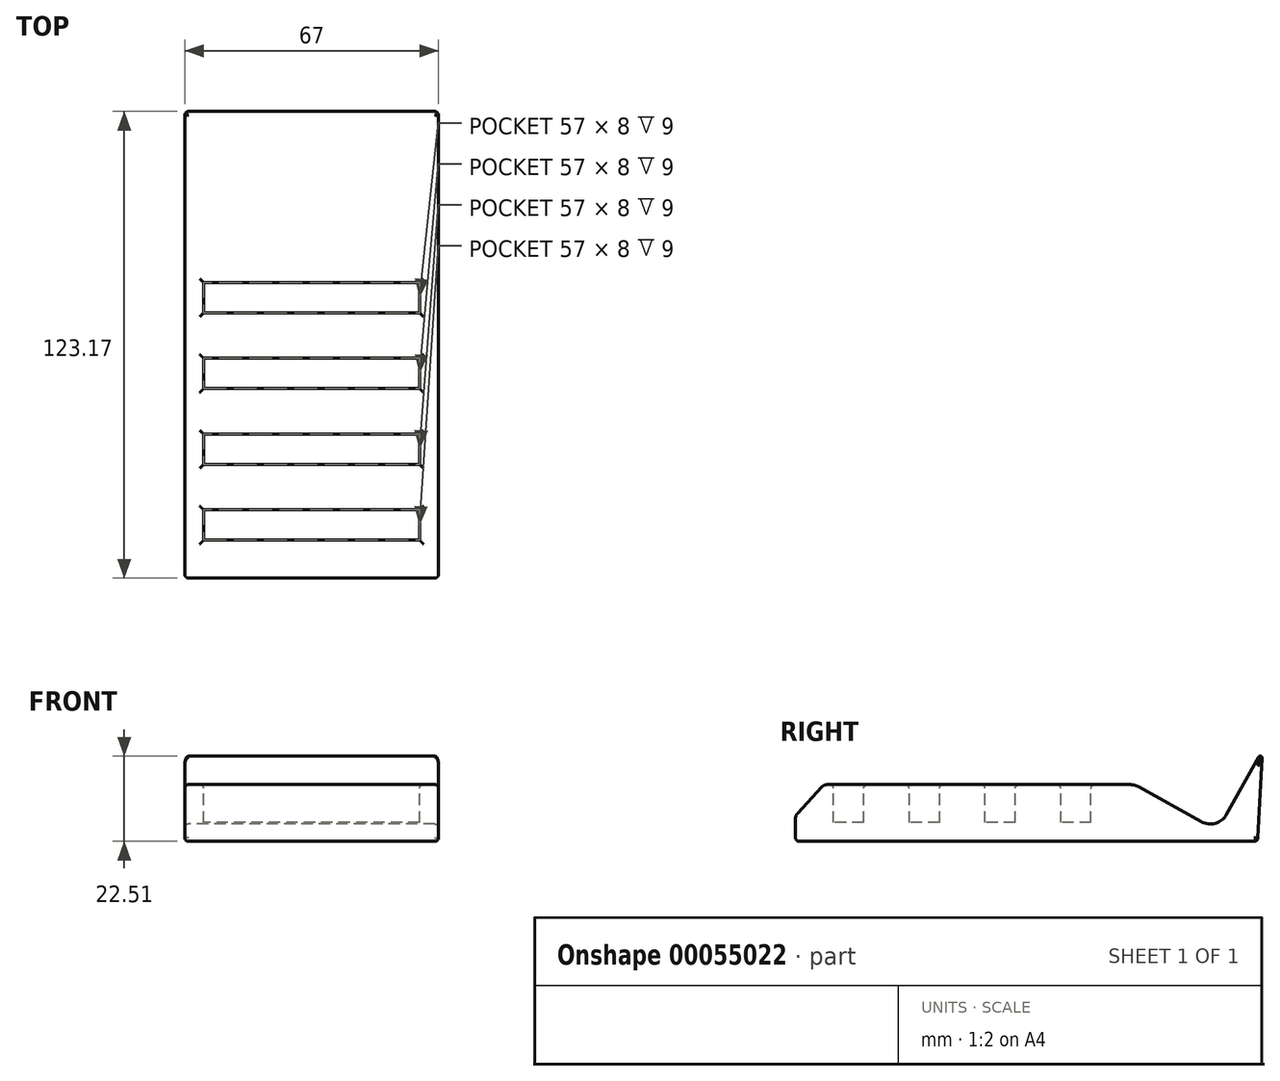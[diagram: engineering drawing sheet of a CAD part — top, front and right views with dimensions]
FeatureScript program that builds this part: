
annotation { "Feature Type Name" : "Feature", "Feature Type Description" : "" }
export const myFeature = defineFeature(function(context is Context, id is Id, definition is map)
    precondition{}
    {
        {
            var Q0;
            Q0=qCreatedBy(makeId("Right.planeOp"),FACE);
            var sketch = newSketch(context, id + "F0", { "sketchPlane" : qUnion([Q0])});
            skLineSegment(sketch, "E0.rect.bottom", {"start": v(27.22, 7.5) * mm, "end": v(-52.62, 7.5) * mm});
            skLineSegment(sketch, "E0.rect.top", {"start": v(61, -7.5) * mm, "end": v(-61, -7.5) * mm});
            skLineSegment(sketch, "E0.rect.right", {"start": v(-61, -1.4) * mm, "end": v(-61, -7.5) * mm});
            skPoint(sketch, "E0.rect.middle", {"position": v(0, 0) * mm});
            skLineSegment(sketch, "E1", {"start": v(45.97, -2.27) * mm, "end": v(29.66, 6.86) * mm});
            skLineSegment(sketch, "E2", {"start": v(52.78, -0.35) * mm, "end": v(61.24, 14.76) * mm});
            skLineSegment(sketch, "E3", {"start": v(61, -7.5) * mm, "end": v(62.17, 14.49) * mm});
            skPoint(sketch, "E4.visualSharp", {"position": v(62.29, 16.63) * mm});
            skArc(sketch, "E4.filletArc", {"start": v(62.17, 14.49) * mm, "mid": v(61.81, 15) * mm, "end": v(61.24, 14.76) * mm});
            skPoint(sketch, "E5.visualSharp", {"position": v(28.52, 7.5) * mm});
            skArc(sketch, "E5.filletArc", {"start": v(29.66, 6.86) * mm, "mid": v(28.48, 7.34) * mm, "end": v(27.22, 7.5) * mm});
            skPoint(sketch, "E6.visualSharp", {"position": v(50.33, -4.72) * mm});
            skArc(sketch, "E6.filletArc", {"start": v(45.97, -2.27) * mm, "mid": v(49.77, -2.72) * mm, "end": v(52.78, -0.35) * mm});
            skLineSegment(sketch, "E7", {"start": v(-60.47, -0.05) * mm, "end": v(-54.1, 6.86) * mm});
            skPoint(sketch, "E8.visualSharp", {"position": v(-53.5, 7.5) * mm});
            skArc(sketch, "E8.filletArc", {"start": v(-52.62, 7.5) * mm, "mid": v(-53.43, 7.33) * mm, "end": v(-54.1, 6.86) * mm});
            skPoint(sketch, "E9.visualSharp", {"position": v(-61, -0.62) * mm});
            skArc(sketch, "E9.filletArc", {"start": v(-60.47, -0.05) * mm, "mid": v(-60.86, -0.67) * mm, "end": v(-61, -1.4) * mm});
            skSolve(sketch);
        }
        {
            var Q0;
            Q0=makeQuery(id+"F0.imprint","IMPRINT",FACE,{"disambiguationData":[TD([[makeQuery(id+"F0.imprint","IMPRINT",EDGE,{"derivedFrom":sQuery(id+"F0.wireOp",EDGE,"E0.rect.bottom")}),1.0]])]});
            extrude(context, id + "F1", {"entities" : qUnion([Q0]), "depth" : 33.5 * mm, "hasSecondDirection" : true, "secondDirectionOppositeDirection" : true, "secondDirectionDepth" : 33.5 * mm});
        }
        {
            var Q0;
            Q0=makeQuery(id+"F1.opExtrude","SWEPT_FACE",FACE,{"disambiguationData":[OSD([sQuery(id+"F0.wireOp",EDGE,"E0.rect.bottom")])]});
            var sketch = newSketch(context, id + "F2", { "sketchPlane" : qUnion([Q0])});
            skLineSegment(sketch, "E10.rect.bottom", {"start": v(28.5, -43) * mm, "end": v(-28.5, -43) * mm});
            skLineSegment(sketch, "E10.rect.top", {"start": v(28.5, -51) * mm, "end": v(-28.5, -51) * mm});
            skLineSegment(sketch, "E10.rect.left", {"start": v(28.5, -43) * mm, "end": v(28.5, -51) * mm});
            skLineSegment(sketch, "E10.rect.right", {"start": v(-28.5, -43) * mm, "end": v(-28.5, -51) * mm});
            skPoint(sketch, "E10.rect.middle", {"position": v(0, -47) * mm});
            skPoint(sketch, "E11.rect.middle", {"position": v(0, -27) * mm});
            skLineSegment(sketch, "E11.rect.bottom", {"start": v(28.5, -23) * mm, "end": v(-28.5, -23) * mm});
            skLineSegment(sketch, "E11.rect.right", {"start": v(-28.5, -23) * mm, "end": v(-28.5, -31) * mm});
            skLineSegment(sketch, "E11.rect.left", {"start": v(28.5, -23) * mm, "end": v(28.5, -31) * mm});
            skLineSegment(sketch, "E11.rect.top", {"start": v(28.5, -31) * mm, "end": v(-28.5, -31) * mm});
            skPoint(sketch, "E12.rect.middle", {"position": v(0, -7) * mm});
            skLineSegment(sketch, "E12.rect.bottom", {"start": v(28.5, -3) * mm, "end": v(-28.5, -3) * mm});
            skLineSegment(sketch, "E12.rect.right", {"start": v(-28.5, -3) * mm, "end": v(-28.5, -11) * mm});
            skLineSegment(sketch, "E12.rect.left", {"start": v(28.5, -3) * mm, "end": v(28.5, -11) * mm});
            skLineSegment(sketch, "E12.rect.top", {"start": v(28.5, -11) * mm, "end": v(-28.5, -11) * mm});
            skPoint(sketch, "E13.rect.middle", {"position": v(0, 13) * mm});
            skLineSegment(sketch, "E13.rect.bottom", {"start": v(28.5, 17) * mm, "end": v(-28.5, 17) * mm});
            skLineSegment(sketch, "E13.rect.right", {"start": v(-28.5, 17) * mm, "end": v(-28.5, 9) * mm});
            skLineSegment(sketch, "E13.rect.left", {"start": v(28.5, 17) * mm, "end": v(28.5, 9) * mm});
            skLineSegment(sketch, "E13.rect.top", {"start": v(28.5, 9) * mm, "end": v(-28.5, 9) * mm});
            skSolve(sketch);
        }
        {
            var Q0;
            Q0=makeQuery(id+"F2.imprint","IMPRINT",FACE,{"disambiguationData":[TD([[makeQuery(id+"F2.imprint","IMPRINT",EDGE,{"derivedFrom":sQuery(id+"F2.wireOp",EDGE,"E10.rect.bottom")}),1.0]])]});
            var Q1;
            Q1=makeQuery(id+"F2.imprint","IMPRINT",FACE,{"disambiguationData":[TD([[makeQuery(id+"F2.imprint","IMPRINT",EDGE,{"derivedFrom":sQuery(id+"F2.wireOp",EDGE,"E11.rect.bottom")}),1.0]])]});
            var Q2;
            Q2=makeQuery(id+"F2.imprint","IMPRINT",FACE,{"disambiguationData":[TD([[makeQuery(id+"F2.imprint","IMPRINT",EDGE,{"derivedFrom":sQuery(id+"F2.wireOp",EDGE,"E12.rect.bottom")}),1.0]])]});
            var Q3;
            Q3=makeQuery(id+"F2.imprint","IMPRINT",FACE,{"disambiguationData":[TD([[makeQuery(id+"F2.imprint","IMPRINT",EDGE,{"derivedFrom":sQuery(id+"F2.wireOp",EDGE,"E13.rect.bottom")}),1.0]])]});
            extrude(context, id + "F3", {"entities" : qUnion([Q0, Q1, Q2, Q3]), "operationType" : NewBodyOperationType.REMOVE, "oppositeDirection" : true, "depth" : 10 * mm});
        }
        {
            var Q0;
            Q0=makeQuery(id+"F1.opExtrude","CAP_EDGE",EDGE,{"disambiguationData":[OSD([sQuery(id+"F0.wireOp",EDGE,"E0.rect.bottom")])],"isStart":false});
            var Q1;
            Q1=makeQuery(id+"F1.opExtrude","CAP_EDGE",EDGE,{"disambiguationData":[OSD([sQuery(id+"F0.wireOp",EDGE,"E0.rect.bottom")])],"isStart":true});
            fillet(context, id + "F4", {"entities" : qUnion([Q0, Q1]), "radius" : 1 * mm, "tangentPropagation" : true, "allowEdgeOverflow" : false});
        }
        {
            var Q0;
            Q0=makeQuery(id+"F1.opExtrude","SWEPT_FACE",FACE,{"disambiguationData":[OSD([sQuery(id+"F0.wireOp",EDGE,"E0.rect.top")])]});
            fillet(context, id + "F5", {"entities" : qUnion([Q0]), "radius" : 1 * mm, "tangentPropagation" : true, "allowEdgeOverflow" : false});
        }
        {
            var Q0;
            Q0=makeQuery(id+"F1.opExtrude","SWEPT_FACE",FACE,{"disambiguationData":[OSD([sQuery(id+"F0.wireOp",EDGE,"E0.rect.bottom")])]});
            fillet(context, id + "F6", {"entities" : qUnion([Q0]), "radius" : 1 * mm, "tangentPropagation" : true, "allowEdgeOverflow" : false});
        }
    });
